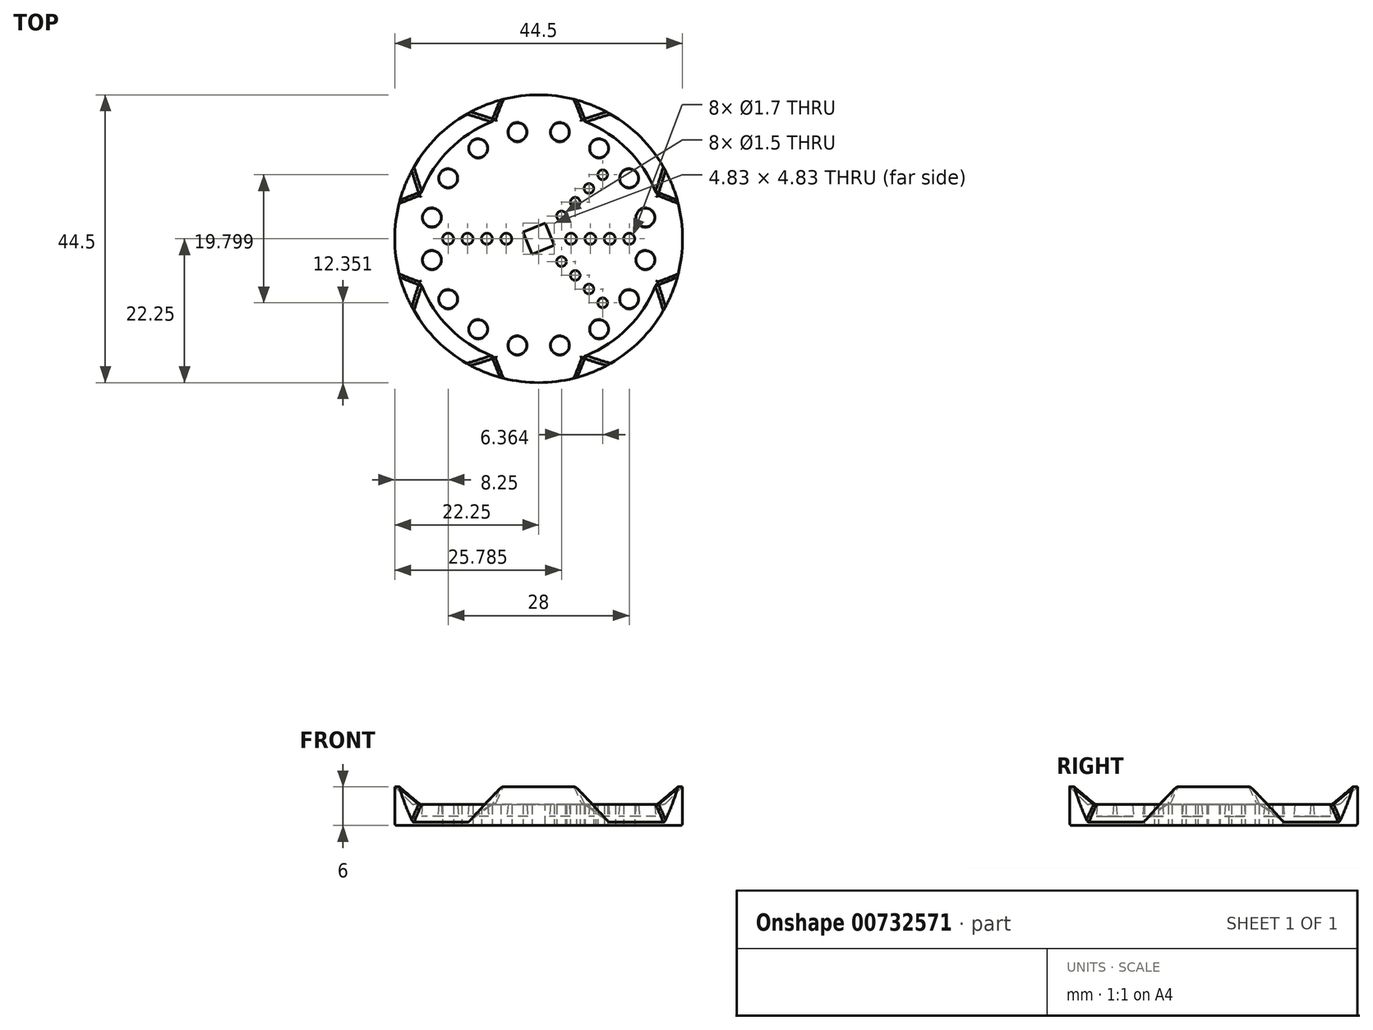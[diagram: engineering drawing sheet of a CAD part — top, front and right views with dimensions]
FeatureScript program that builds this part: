
annotation { "Feature Type Name" : "Feature", "Feature Type Description" : "" }
export const myFeature = defineFeature(function(context is Context, id is Id, definition is map)
    precondition{}
    {
        {
            assignVariable(context, id + "F0", {"name" : "AlignmentGuide", "anyValue" : 2.75});
        }
        {
            assignVariable(context, id + "F1", {"name" : "AlignmentRail", "anyValue" : .5});
        }
        {
            assignVariable(context, id + "F2", {"name" : "AlignmentSpacing", "anyValue" : .25});
        }
        {
            var Q0;
            Q0=qCreatedBy(makeId("Top.planeOp"),FACE);
            var sketch = newSketch(context, id + "F3", { "sketchPlane" : qUnion([Q0])});
            skCircle(sketch, "E0", {"center": v(0, 0) * mm, "radius": 19.5 * mm});
            skCircle(sketch, "E1", {"center": v(5, 0) * mm, "radius": 0.85 * mm});
            skCircle(sketch, "E2", {"center": v(8, 0) * mm, "radius": 0.85 * mm});
            skCircle(sketch, "E3", {"center": v(11, 0) * mm, "radius": 0.85 * mm});
            skCircle(sketch, "E4", {"center": v(14, 0) * mm, "radius": 0.85 * mm});
            skLineSegment(sketch, "E5", {"start": v(2, 0) * mm, "end": v(1.41, 1.41) * mm});
            skLineSegment(sketch, "E6", {"start": v(1.41, -1.41) * mm, "end": v(2, 0) * mm, "construction": true});
            skLineSegment(sketch, "E7", {"start": v(1.7, 0.7) * mm, "end": v(18.02, 7.46) * mm, "construction": true});
            skCircle(sketch, "E8.1.0", {"center": v(-5, 0) * mm, "radius": 0.85 * mm});
            skCircle(sketch, "E8.1.1", {"center": v(-8, 0) * mm, "radius": 0.85 * mm});
            skCircle(sketch, "E8.1.2", {"center": v(-11, 0) * mm, "radius": 0.85 * mm});
            skCircle(sketch, "E8.1.3", {"center": v(-14, 0) * mm, "radius": 0.85 * mm});
            skLineSegment(sketch, "E9", {"start": v(19.5, 0) * mm, "end": v(22.25, 0) * mm, "construction": true});
            skLineSegment(sketch, "E10", {"start": v(18.02, 7.46) * mm, "end": v(17.04, 9.49) * mm, "construction": true});
            skLineSegment(sketch, "E11", {"start": v(18.02, -7.46) * mm, "end": v(17.04, -9.49) * mm, "construction": true});
            skLineSegment(sketch, "E12", {"start": v(17.04, 9.49) * mm, "end": v(19.44, 10.83) * mm});
            skArc(sketch, "E13", {"start": v(19.44, 10.83) * mm, "mid": v(21.54, 5.6) * mm, "end": v(22.25, 0) * mm});
            skLineSegment(sketch, "E14", {"start": v(20.53, 8.86) * mm, "end": v(19.44, 10.83) * mm, "construction": true});
            skArc(sketch, "E15", {"start": v(22.25, 0) * mm, "mid": v(21.54, -5.6) * mm, "end": v(19.44, -10.83) * mm});
            skLineSegment(sketch, "E16", {"start": v(17.04, -9.49) * mm, "end": v(19.44, -10.83) * mm});
            skLineSegment(sketch, "E17", {"start": v(20.53, -8.86) * mm, "end": v(19.44, -10.83) * mm, "construction": true});
            skLineSegment(sketch, "E18", {"start": v(19.44, -10.83) * mm, "end": v(21.84, -12.16) * mm});
            skLineSegment(sketch, "E19", {"start": v(19.44, 10.83) * mm, "end": v(21.84, 12.16) * mm});
            skLineSegment(sketch, "E20", {"start": v(22.25, 0) * mm, "end": v(25, 0) * mm, "construction": true});
            skArc(sketch, "E21", {"start": v(21.84, -12.16) * mm, "mid": v(25, 0) * mm, "end": v(21.84, 12.16) * mm});
            skArc(sketch, "E22", {"start": v(19.44, 10.83) * mm, "mid": v(-22.25, 0) * mm, "end": v(19.44, -10.83) * mm});
            skLineSegment(sketch, "E23", {"start": v(0, 2) * mm, "end": v(0, 19.5) * mm, "construction": true});
            skLineSegment(sketch, "E24", {"start": v(0, 0) * mm, "end": v(0.85, 0) * mm, "construction": true});
            skLineSegment(sketch, "E25", {"start": v(0, 2) * mm, "end": v(1.41, 1.41) * mm, "construction": true});
            skLineSegment(sketch, "E26", {"start": v(0, 0) * mm, "end": v(-0.53, 0.53) * mm, "construction": true});
            skCircle(sketch, "E27", {"center": v(3.54, -3.54) * mm, "radius": 0.75 * mm});
            skLineSegment(sketch, "E28", {"start": v(5, 0) * mm, "end": v(8, 0) * mm, "construction": true});
            skLineSegment(sketch, "E29", {"start": v(8, 0) * mm, "end": v(11, 0) * mm, "construction": true});
            skLineSegment(sketch, "E30", {"start": v(11, 0) * mm, "end": v(14, 0) * mm, "construction": true});
            skLineSegment(sketch, "E31", {"start": v(5, 0) * mm, "end": v(5, 0.85) * mm, "construction": true});
            skLineSegment(sketch, "E32", {"start": v(3.54, -3.54) * mm, "end": v(3, -4.07) * mm, "construction": true});
            skLineSegment(sketch, "E33", {"start": v(3.54, -3.54) * mm, "end": v(5.66, -5.66) * mm, "construction": true});
            skLineSegment(sketch, "E34", {"start": v(5.66, -5.66) * mm, "end": v(7.78, -7.78) * mm, "construction": true});
            skLineSegment(sketch, "E35", {"start": v(7.78, -7.78) * mm, "end": v(9.9, -9.9) * mm, "construction": true});
            skCircle(sketch, "E36", {"center": v(5.66, -5.66) * mm, "radius": 0.75 * mm});
            skCircle(sketch, "E37", {"center": v(7.78, -7.78) * mm, "radius": 0.75 * mm});
            skCircle(sketch, "E38", {"center": v(9.9, -9.9) * mm, "radius": 0.75 * mm});
            skCircle(sketch, "E39.1.0", {"center": v(3.54, 3.54) * mm, "radius": 0.75 * mm});
            skCircle(sketch, "E39.1.1", {"center": v(5.66, 5.66) * mm, "radius": 0.75 * mm});
            skCircle(sketch, "E39.1.2", {"center": v(7.78, 7.78) * mm, "radius": 0.75 * mm});
            skCircle(sketch, "E39.1.3", {"center": v(9.9, 9.9) * mm, "radius": 0.75 * mm});
            skLineSegment(sketch, "E40", {"start": v(2, 0) * mm, "end": v(5, 0) * mm, "construction": true});
            skLineSegment(sketch, "E41", {"start": v(1.41, -1.41) * mm, "end": v(3.54, -3.54) * mm, "construction": true});
            skLineSegment(sketch, "E42", {"start": v(0, 0) * mm, "end": v(0, 2) * mm});
            skLineSegment(sketch, "E43", {"start": v(0, 0) * mm, "end": v(1.41, 1.41) * mm});
            skCircle(sketch, "E44.1.2.0", {"center": v(-3.54, 3.54) * mm, "radius": 0.75 * mm});
            skCircle(sketch, "E44.2.2.0", {"center": v(-5.66, 5.66) * mm, "radius": 0.75 * mm});
            skCircle(sketch, "E44.4.2.0", {"center": v(-7.78, 7.78) * mm, "radius": 0.75 * mm});
            skCircle(sketch, "E44.6.2.0", {"center": v(-9.9, 9.9) * mm, "radius": 0.75 * mm});
            skCircle(sketch, "E44.1.3.0", {"center": v(-3.54, -3.54) * mm, "radius": 0.75 * mm});
            skCircle(sketch, "E44.2.3.0", {"center": v(-5.66, -5.66) * mm, "radius": 0.75 * mm});
            skCircle(sketch, "E44.4.3.0", {"center": v(-7.78, -7.78) * mm, "radius": 0.75 * mm});
            skCircle(sketch, "E44.6.3.0", {"center": v(-9.9, -9.9) * mm, "radius": 0.75 * mm});
            skLineSegment(sketch, "E45", {"start": v(0, 0) * mm, "end": v(0, -2) * mm, "construction": true});
            skLineSegment(sketch, "E46", {"start": v(0, -2) * mm, "end": v(1.41, -1.41) * mm});
            skLineSegment(sketch, "E47", {"start": v(0, 0) * mm, "end": v(1.41, -1.41) * mm, "construction": true});
            skLineSegment(sketch, "E48", {"start": v(1.7, -0.7) * mm, "end": v(18.02, -7.46) * mm, "construction": true});
            skLineSegment(sketch, "E49", {"start": v(0, -2) * mm, "end": v(-1.41, -1.41) * mm, "construction": true});
            skLineSegment(sketch, "E50", {"start": v(-1.41, -1.41) * mm, "end": v(-2, 0) * mm});
            skLineSegment(sketch, "E51", {"start": v(-2, 0) * mm, "end": v(-1.41, 1.41) * mm, "construction": true});
            skLineSegment(sketch, "E52", {"start": v(-1.41, 1.41) * mm, "end": v(0, 2) * mm});
            skLineSegment(sketch, "E53", {"start": v(2, 0) * mm, "end": v(2.41, -1) * mm});
            skLineSegment(sketch, "E54", {"start": v(2.41, -1) * mm, "end": v(1.41, -1.41) * mm});
            skLineSegment(sketch, "E55", {"start": v(0, -2) * mm, "end": v(-1, -2.41) * mm});
            skLineSegment(sketch, "E56", {"start": v(-1, -2.41) * mm, "end": v(-1.41, -1.41) * mm});
            skLineSegment(sketch, "E57", {"start": v(-2, 0) * mm, "end": v(-2.41, 1) * mm});
            skLineSegment(sketch, "E58", {"start": v(-2.41, 1) * mm, "end": v(-1.41, 1.41) * mm});
            skLineSegment(sketch, "E59", {"start": v(0, 2) * mm, "end": v(1, 2.41) * mm});
            skLineSegment(sketch, "E60", {"start": v(1, 2.41) * mm, "end": v(1.41, 1.41) * mm});
            skSolve(sketch);
        }
        {
            var Q0;
            Q0=makeQuery(id+"F3.imprint","IMPRINT",FACE,{"disambiguationData":[TD([[makeQuery(id+"F3.imprint","IMPRINT",EDGE,{"derivedFrom":sQuery(id+"F3.wireOp",EDGE,"E0")}),1.0]])]});
            var Q1;
            Q1=makeQuery(id+"F3.imprint","IMPRINT",FACE,{"disambiguationData":[TD([[makeQuery(id+"F3.imprint","IMPRINT",EDGE,{"derivedFrom":sQuery(id+"F3.wireOp",EDGE,"E1")}),-1.0]])]});
            var Q2;
            {var subQ0=sQuery(id+"F3.wireOp",EDGE,"lLyj6t6n-eD48-rOr1-jQWX-CAubWbmxff8s");Q2=makeQuery(id+"F3.imprint","IMPRINT",FACE,{"disambiguationData":[TD([[makeQuery(id+"F3.imprint","IMPRINT",EDGE,{"derivedFrom":subQ0}),-1.0]])]});}
            var Q3;
            {var subQ0=sQuery(id+"F3.wireOp",EDGE,"lLyj6t6n-eD48-rOr1-jQWX-CAubWbmxff8s");Q3=makeQuery(id+"F3.imprint","IMPRINT",FACE,{"disambiguationData":[TD([[makeQuery(id+"F3.imprint","IMPRINT",EDGE,{"derivedFrom":subQ0}),1.0]])]});}
            var Q4;
            {var subQ0=sQuery(id+"F3.wireOp",EDGE,"E12");Q4=makeQuery(id+"F3.imprint","IMPRINT",FACE,{"disambiguationData":[TD([[makeQuery(id+"F3.imprint","IMPRINT",EDGE,{"derivedFrom":subQ0}),-1.0]])]});}
            var Q5;
            {var subQ0=sQuery(id+"F3.wireOp",EDGE,"E12");Q5=makeQuery(id+"F3.imprint","IMPRINT",FACE,{"disambiguationData":[TD([[makeQuery(id+"F3.imprint","IMPRINT",EDGE,{"derivedFrom":subQ0}),1.0]])]});}
            var Q6;
            {var subQ0=sQuery(id+"F3.wireOp",EDGE,"X5LFDRDO-lWhr-AfW1-3y8W-V0I3BShnL0UQ");Q6=makeQuery(id+"F3.imprint","IMPRINT",FACE,{"disambiguationData":[TD([[makeQuery(id+"F3.imprint","IMPRINT",EDGE,{"derivedFrom":subQ0}),1.0]])]});}
            var Q7;
            {var subQ0=sQuery(id+"F3.wireOp",EDGE,"E42");Q7=makeQuery(id+"F3.imprint","IMPRINT",FACE,{"disambiguationData":[TD([[makeQuery(id+"F3.imprint","IMPRINT",EDGE,{"derivedFrom":subQ0}),-1.0]])]});}
            var Q8;
            Q8=makeQuery(id+"F3.imprint","IMPRINT",FACE,{"disambiguationData":[TD([[makeQuery(id+"F3.imprint","IMPRINT",EDGE,{"derivedFrom":sQuery(id+"F3.wireOp",EDGE,"E44.1.3.0")}),1.0]])]});
            var Q9;
            Q9=makeQuery(id+"F3.imprint","IMPRINT",FACE,{"disambiguationData":[TD([[makeQuery(id+"F3.imprint","IMPRINT",EDGE,{"derivedFrom":sQuery(id+"F3.wireOp",EDGE,"E44.2.3.0")}),1.0]])]});
            var Q10;
            Q10=makeQuery(id+"F3.imprint","IMPRINT",FACE,{"disambiguationData":[TD([[makeQuery(id+"F3.imprint","IMPRINT",EDGE,{"derivedFrom":sQuery(id+"F3.wireOp",EDGE,"E44.4.3.0")}),1.0]])]});
            var Q11;
            Q11=makeQuery(id+"F3.imprint","IMPRINT",FACE,{"disambiguationData":[TD([[makeQuery(id+"F3.imprint","IMPRINT",EDGE,{"derivedFrom":sQuery(id+"F3.wireOp",EDGE,"E44.6.3.0")}),1.0]])]});
            var Q12;
            Q12=makeQuery(id+"F3.imprint","IMPRINT",FACE,{"disambiguationData":[TD([[makeQuery(id+"F3.imprint","IMPRINT",EDGE,{"derivedFrom":sQuery(id+"F3.wireOp",EDGE,"E44.1.2.0")}),1.0]])]});
            var Q13;
            Q13=makeQuery(id+"F3.imprint","IMPRINT",FACE,{"disambiguationData":[TD([[makeQuery(id+"F3.imprint","IMPRINT",EDGE,{"derivedFrom":sQuery(id+"F3.wireOp",EDGE,"E44.6.2.0")}),1.0]])]});
            var Q14;
            Q14=makeQuery(id+"F3.imprint","IMPRINT",FACE,{"disambiguationData":[TD([[makeQuery(id+"F3.imprint","IMPRINT",EDGE,{"derivedFrom":sQuery(id+"F3.wireOp",EDGE,"E44.2.2.0")}),1.0]])]});
            var Q15;
            Q15=makeQuery(id+"F3.imprint","IMPRINT",FACE,{"disambiguationData":[TD([[makeQuery(id+"F3.imprint","IMPRINT",EDGE,{"derivedFrom":sQuery(id+"F3.wireOp",EDGE,"E44.4.2.0")}),1.0]])]});
            extrude(context, id + "F4", {"entities" : qUnion([Q0, Q1, Q2, Q3, Q4, Q5, Q6, Q7, Q8, Q9, Q10, Q11, Q12, Q13, Q14, Q15]), "depth" : (getVariable(context, 'AlignmentGuide') + getVariable(context, 'AlignmentRail')) * mm, "offsetDistance" : 25 * mm});
        }
        {
            var Q0;
            Q0=makeQuery(id+"F4.opExtrude","CAP_EDGE",EDGE,{"disambiguationData":[OSD([sQuery(id+"F3.wireOp",EDGE,"E13"),sQuery(id+"F3.wireOp",EDGE,"E15"),sQuery(id+"F3.wireOp",EDGE,"E22")])],"isStart":false});
            chamfer(context, id + "F5", {"entities" : qUnion([Q0]), "width" : (getVariable(context, 'AlignmentGuide')) * mm, "tangentPropagation" : true});
        }
        {
            var Q0;
            {var subQ0=sQuery(id+"F3.wireOp",EDGE,"E12");Q0=makeQuery(id+"F3.imprint","IMPRINT",FACE,{"disambiguationData":[TD([[makeQuery(id+"F3.imprint","IMPRINT",EDGE,{"derivedFrom":subQ0}),-1.0]])]});}
            var Q1;
            Q1=makeQuery(id+"F3.imprint","IMPRINT",FACE,{"disambiguationData":[TD([[makeQuery(id+"F3.imprint","IMPRINT",EDGE,{"derivedFrom":sQuery(id+"F3.wireOp",EDGE,"E13")}),1.0]])]});
            extrude(context, id + "F6", {"entities" : qUnion([Q0, Q1]), "depth" : (getVariable(context, 'AlignmentSpacing') + getVariable(context, 'AlignmentGuide') * 2 + getVariable(context, 'AlignmentRail') * 2) * mm, "offsetDistance" : 25 * mm});
        }
        {
            var Q0;
            Q0=makeQuery(id+"F6.opExtrude","CAP_EDGE",EDGE,{"disambiguationData":[OSD([sQuery(id+"F3.wireOp",EDGE,"E16"),sQuery(id+"F3.wireOp",EDGE,"E18")])],"isStart":false});
            var Q1;
            Q1=makeQuery(id+"F6.opExtrude","CAP_EDGE",EDGE,{"disambiguationData":[OSD([sQuery(id+"F3.wireOp",EDGE,"E12"),sQuery(id+"F3.wireOp",EDGE,"E19")])],"isStart":false});
            chamfer(context, id + "F7", {"entities" : qUnion([Q0, Q1]), "width" : (getVariable(context, 'AlignmentGuide') * 2 + getVariable(context, 'AlignmentSpacing') + getVariable(context, 'AlignmentRail')) * mm, "tangentPropagation" : true});
        }
        {
            var Q0;
            Q0=makeQuery(id+"F6.opExtrude","CAP_EDGE",EDGE,{"disambiguationData":[OSD([sQuery(id+"F3.wireOp",EDGE,"ykJoU9iX-xNW1-ZPCr-MGLN-cVTnYyaPD16A")])],"isStart":false});
            var Q1;
            Q1=makeQuery(id+"F6.opExtrude","CAP_EDGE",EDGE,{"disambiguationData":[OSD([sQuery(id+"F3.wireOp",EDGE,"lLyj6t6n-eD48-rOr1-jQWX-CAubWbmxff8s")])],"isStart":false});
            var Q2;
            Q2=makeQuery(id+"F6.opExtrude","CAP_EDGE",EDGE,{"disambiguationData":[OSD([sQuery(id+"F3.wireOp",EDGE,"E0")])],"isStart":false});
            chamfer(context, id + "F8", {"entities" : qUnion([Q0, Q1, Q2]), "width" : (getVariable(context, 'AlignmentGuide') + getVariable(context, 'AlignmentSpacing') + getVariable(context, 'AlignmentRail')) * mm, "tangentPropagation" : true});
        }
        {
            var Q0;
            Q0=makeQuery(id+"F8.opChamfer","BLEND_EDGE",EDGE,{"blendedFrom":[makeQuery(id+"F6.opExtrude","CAP_EDGE",EDGE,{"disambiguationData":[OSD([sQuery(id+"F3.wireOp",EDGE,"E0")])],"isStart":false}),makeQuery(id+"F7.opChamfer","BLEND_FACE",FACE,{"disambiguationData":[OSD([sQuery(id+"F3.wireOp",EDGE,"E16"),sQuery(id+"F3.wireOp",EDGE,"E18")])]})],"blendedInto":[makeQuery(id+"F7.opChamfer","BLEND_FACE",FACE,{"disambiguationData":[OSD([sQuery(id+"F3.wireOp",EDGE,"E16"),sQuery(id+"F3.wireOp",EDGE,"E18")])]})]});
            var Q1;
            {var subQ0=sQuery(id+"F3.wireOp",EDGE,"E18");var subQ1=sQuery(id+"F3.wireOp",EDGE,"E16");Q1=makeQuery(id+"F7.opChamfer","BLEND_EDGE",EDGE,{"blendedFrom":[makeQuery(id+"F6.opExtrude","CAP_EDGE",EDGE,{"disambiguationData":[OSD([subQ1,subQ0])],"isStart":false}),makeQuery(id+"F6.opExtrude","CAP_FACE",FACE,{"disambiguationData":[OSD([sQuery(id+"F3.wireOp",EDGE,"E0"),sQuery(id+"F3.wireOp",EDGE,"E12"),subQ1,subQ0,sQuery(id+"F3.wireOp",EDGE,"E19"),sQuery(id+"F3.wireOp",EDGE,"E21")])],"isStart":false})],"blendedInto":[makeQuery(id+"F6.opExtrude","CAP_FACE",FACE,{"disambiguationData":[OSD([sQuery(id+"F3.wireOp",EDGE,"E0"),sQuery(id+"F3.wireOp",EDGE,"E12"),subQ1,subQ0,sQuery(id+"F3.wireOp",EDGE,"E19"),sQuery(id+"F3.wireOp",EDGE,"E21")])],"isStart":false})]});}
            var Q2;
            {var subQ0=sQuery(id+"F3.wireOp",EDGE,"E0");Q2=makeQuery(id+"F8.opChamfer","BLEND_EDGE",EDGE,{"blendedFrom":[makeQuery(id+"F6.opExtrude","CAP_EDGE",EDGE,{"disambiguationData":[OSD([subQ0])],"isStart":false}),makeQuery(id+"F6.opExtrude","CAP_FACE",FACE,{"disambiguationData":[OSD([subQ0,sQuery(id+"F3.wireOp",EDGE,"E12"),sQuery(id+"F3.wireOp",EDGE,"E16"),sQuery(id+"F3.wireOp",EDGE,"E18"),sQuery(id+"F3.wireOp",EDGE,"E19"),sQuery(id+"F3.wireOp",EDGE,"E21")])],"isStart":false})],"blendedInto":[makeQuery(id+"F6.opExtrude","CAP_FACE",FACE,{"disambiguationData":[OSD([subQ0,sQuery(id+"F3.wireOp",EDGE,"E12"),sQuery(id+"F3.wireOp",EDGE,"E16"),sQuery(id+"F3.wireOp",EDGE,"E18"),sQuery(id+"F3.wireOp",EDGE,"E19"),sQuery(id+"F3.wireOp",EDGE,"E21")])],"isStart":false})]});}
            var Q3;
            Q3=makeQuery(id+"F8.opChamfer","BLEND_EDGE",EDGE,{"blendedFrom":[makeQuery(id+"F6.opExtrude","CAP_EDGE",EDGE,{"disambiguationData":[OSD([sQuery(id+"F3.wireOp",EDGE,"E0")])],"isStart":false}),makeQuery(id+"F7.opChamfer","BLEND_FACE",FACE,{"disambiguationData":[OSD([sQuery(id+"F3.wireOp",EDGE,"E12"),sQuery(id+"F3.wireOp",EDGE,"E19")])]})],"blendedInto":[makeQuery(id+"F7.opChamfer","BLEND_FACE",FACE,{"disambiguationData":[OSD([sQuery(id+"F3.wireOp",EDGE,"E12"),sQuery(id+"F3.wireOp",EDGE,"E19")])]})]});
            var Q4;
            {var subQ0=sQuery(id+"F3.wireOp",EDGE,"E19");var subQ1=sQuery(id+"F3.wireOp",EDGE,"E12");Q4=makeQuery(id+"F7.opChamfer","BLEND_EDGE",EDGE,{"blendedFrom":[makeQuery(id+"F6.opExtrude","CAP_EDGE",EDGE,{"disambiguationData":[OSD([subQ1,subQ0])],"isStart":false}),makeQuery(id+"F6.opExtrude","CAP_FACE",FACE,{"disambiguationData":[OSD([sQuery(id+"F3.wireOp",EDGE,"E0"),subQ1,sQuery(id+"F3.wireOp",EDGE,"E16"),sQuery(id+"F3.wireOp",EDGE,"E18"),subQ0,sQuery(id+"F3.wireOp",EDGE,"E21")])],"isStart":false})],"blendedInto":[makeQuery(id+"F6.opExtrude","CAP_FACE",FACE,{"disambiguationData":[OSD([sQuery(id+"F3.wireOp",EDGE,"E0"),subQ1,sQuery(id+"F3.wireOp",EDGE,"E16"),sQuery(id+"F3.wireOp",EDGE,"E18"),subQ0,sQuery(id+"F3.wireOp",EDGE,"E21")])],"isStart":false})]});}
            var Q5;
            Q5=makeQuery(id+"F6.opExtrude","CAP_EDGE",EDGE,{"disambiguationData":[OSD([sQuery(id+"F3.wireOp",EDGE,"E21")])],"isStart":false});
            var Q6;
            Q6=makeQuery(id+"F7.opChamfer","BLEND_EDGE",EDGE,{"blendedFrom":[makeQuery(id+"F6.opExtrude","CAP_EDGE",EDGE,{"disambiguationData":[OSD([sQuery(id+"F3.wireOp",EDGE,"E16"),sQuery(id+"F3.wireOp",EDGE,"E18")])],"isStart":false}),makeQuery(id+"F6.opExtrude","SWEPT_FACE",FACE,{"disambiguationData":[OSD([sQuery(id+"F3.wireOp",EDGE,"E21")])]})],"blendedInto":[makeQuery(id+"F6.opExtrude","SWEPT_FACE",FACE,{"disambiguationData":[OSD([sQuery(id+"F3.wireOp",EDGE,"E21")])]})]});
            var Q7;
            Q7=makeQuery(id+"F7.opChamfer","BLEND_EDGE",EDGE,{"blendedFrom":[makeQuery(id+"F6.opExtrude","CAP_EDGE",EDGE,{"disambiguationData":[OSD([sQuery(id+"F3.wireOp",EDGE,"E12"),sQuery(id+"F3.wireOp",EDGE,"E19")])],"isStart":false}),makeQuery(id+"F6.opExtrude","SWEPT_FACE",FACE,{"disambiguationData":[OSD([sQuery(id+"F3.wireOp",EDGE,"E21")])]})],"blendedInto":[makeQuery(id+"F6.opExtrude","SWEPT_FACE",FACE,{"disambiguationData":[OSD([sQuery(id+"F3.wireOp",EDGE,"E21")])]})]});
            fillet(context, id + "F9", {"entities" : qUnion([Q0, Q1, Q2, Q3, Q4, Q5, Q6, Q7]), "radius" : .5 * mm, "tangentPropagation" : true, "allowEdgeOverflow" : false});
        }
        {
            var Q0;
            Q0=makeQuery(id+"F6.opExtrude","SWEPT_BODY",BODY,{"disambiguationData":[OSD([sQuery(id+"F3.wireOp",EDGE,"E0"),sQuery(id+"F3.wireOp",EDGE,"E12"),sQuery(id+"F3.wireOp",EDGE,"E16"),sQuery(id+"F3.wireOp",EDGE,"E18"),sQuery(id+"F3.wireOp",EDGE,"E19"),sQuery(id+"F3.wireOp",EDGE,"E21")])]});
            var Q1;
            Q1=makeQuery(id+"F4.opExtrude","SWEPT_EDGE",EDGE,{"disambiguationData":[OSD([sQuery(id+"F3.wireOp",EDGE,"E42"),sQuery(id+"F3.wireOp",EDGE,"E43")])]});
            circularPattern(context, id + "F10", {"operationType" : NewBodyOperationType.ADD, "entities" : qUnion([Q0]), "axis" : qUnion([Q1]), "angle" : 360 * degree, "instanceCount" : 4, "equalSpace" : true});
        }
        {
            var Q0;
            {var subQ0=sQuery(id+"F3.wireOp",EDGE,"E42");Q0=makeQuery(id+"F3.imprint","IMPRINT",FACE,{"disambiguationData":[TD([[makeQuery(id+"F3.imprint","IMPRINT",EDGE,{"derivedFrom":subQ0}),-1.0]])]});}
            extrude(context, id + "F11", {"entities" : qUnion([Q0]), "operationType" : NewBodyOperationType.REMOVE, "oppositeDirection" : true, "depth" : 25 * mm, "offsetDistance" : 25 * mm, "hasSecondDirection" : true, "secondDirectionOppositeDirection" : false, "secondDirectionDepth" : 25 * mm});
        }
        {
            var Q0;
            Q0=makeQuery(id+"F10.boolean.opBoolean","INTERSECT",EDGE,{"derivedFrom":[makeQuery(id+"F5.opChamfer","BLEND_FACE",FACE,{"disambiguationData":[OSD([sQuery(id+"F3.wireOp",EDGE,"E13"),sQuery(id+"F3.wireOp",EDGE,"E15"),sQuery(id+"F3.wireOp",EDGE,"E22")])]}),makeQuery(id+"F10.opPattern","COPY",FACE,{"derivedFrom":makeQuery(id+"F7.opChamfer","BLEND_FACE",FACE,{"disambiguationData":[OSD([sQuery(id+"F3.wireOp",EDGE,"E16"),sQuery(id+"F3.wireOp",EDGE,"E18")])]}),"instanceName":"3"})]});
            var Q1;
            Q1=makeQuery(id+"F10.boolean.opBoolean","INTERSECT",EDGE,{"derivedFrom":[makeQuery(id+"F5.opChamfer","BLEND_FACE",FACE,{"disambiguationData":[OSD([sQuery(id+"F3.wireOp",EDGE,"E13"),sQuery(id+"F3.wireOp",EDGE,"E15"),sQuery(id+"F3.wireOp",EDGE,"E22")])]}),makeQuery(id+"F7.opChamfer","BLEND_FACE",FACE,{"disambiguationData":[OSD([sQuery(id+"F3.wireOp",EDGE,"E12"),sQuery(id+"F3.wireOp",EDGE,"E19")])]})]});
            var Q2;
            Q2=makeQuery(id+"F10.boolean.opBoolean","INTERSECT",EDGE,{"derivedFrom":[makeQuery(id+"F5.opChamfer","BLEND_FACE",FACE,{"disambiguationData":[OSD([sQuery(id+"F3.wireOp",EDGE,"E13"),sQuery(id+"F3.wireOp",EDGE,"E15"),sQuery(id+"F3.wireOp",EDGE,"E22")])]}),makeQuery(id+"F7.opChamfer","BLEND_FACE",FACE,{"disambiguationData":[OSD([sQuery(id+"F3.wireOp",EDGE,"E16"),sQuery(id+"F3.wireOp",EDGE,"E18")])]})]});
            var Q3;
            Q3=makeQuery(id+"F10.boolean.opBoolean","INTERSECT",EDGE,{"derivedFrom":[makeQuery(id+"F5.opChamfer","BLEND_FACE",FACE,{"disambiguationData":[OSD([sQuery(id+"F3.wireOp",EDGE,"E13"),sQuery(id+"F3.wireOp",EDGE,"E15"),sQuery(id+"F3.wireOp",EDGE,"E22")])]}),makeQuery(id+"F10.opPattern","COPY",FACE,{"derivedFrom":makeQuery(id+"F7.opChamfer","BLEND_FACE",FACE,{"disambiguationData":[OSD([sQuery(id+"F3.wireOp",EDGE,"E12"),sQuery(id+"F3.wireOp",EDGE,"E19")])]}),"instanceName":"1"})]});
            var Q4;
            Q4=makeQuery(id+"F10.boolean.opBoolean","INTERSECT",EDGE,{"derivedFrom":[makeQuery(id+"F5.opChamfer","BLEND_FACE",FACE,{"disambiguationData":[OSD([sQuery(id+"F3.wireOp",EDGE,"E13"),sQuery(id+"F3.wireOp",EDGE,"E15"),sQuery(id+"F3.wireOp",EDGE,"E22")])]}),makeQuery(id+"F10.opPattern","COPY",FACE,{"derivedFrom":makeQuery(id+"F7.opChamfer","BLEND_FACE",FACE,{"disambiguationData":[OSD([sQuery(id+"F3.wireOp",EDGE,"E16"),sQuery(id+"F3.wireOp",EDGE,"E18")])]}),"instanceName":"1"})]});
            var Q5;
            Q5=makeQuery(id+"F10.boolean.opBoolean","INTERSECT",EDGE,{"derivedFrom":[makeQuery(id+"F5.opChamfer","BLEND_FACE",FACE,{"disambiguationData":[OSD([sQuery(id+"F3.wireOp",EDGE,"E13"),sQuery(id+"F3.wireOp",EDGE,"E15"),sQuery(id+"F3.wireOp",EDGE,"E22")])]}),makeQuery(id+"F10.opPattern","COPY",FACE,{"derivedFrom":makeQuery(id+"F7.opChamfer","BLEND_FACE",FACE,{"disambiguationData":[OSD([sQuery(id+"F3.wireOp",EDGE,"E12"),sQuery(id+"F3.wireOp",EDGE,"E19")])]}),"instanceName":"2"})]});
            var Q6;
            Q6=makeQuery(id+"F10.boolean.opBoolean","INTERSECT",EDGE,{"derivedFrom":[makeQuery(id+"F5.opChamfer","BLEND_FACE",FACE,{"disambiguationData":[OSD([sQuery(id+"F3.wireOp",EDGE,"E13"),sQuery(id+"F3.wireOp",EDGE,"E15"),sQuery(id+"F3.wireOp",EDGE,"E22")])]}),makeQuery(id+"F10.opPattern","COPY",FACE,{"derivedFrom":makeQuery(id+"F7.opChamfer","BLEND_FACE",FACE,{"disambiguationData":[OSD([sQuery(id+"F3.wireOp",EDGE,"E12"),sQuery(id+"F3.wireOp",EDGE,"E19")])]}),"instanceName":"3"})]});
            var Q7;
            Q7=makeQuery(id+"F10.boolean.opBoolean","INTERSECT",EDGE,{"derivedFrom":[makeQuery(id+"F5.opChamfer","BLEND_FACE",FACE,{"disambiguationData":[OSD([sQuery(id+"F3.wireOp",EDGE,"E13"),sQuery(id+"F3.wireOp",EDGE,"E15"),sQuery(id+"F3.wireOp",EDGE,"E22")])]}),makeQuery(id+"F10.opPattern","COPY",FACE,{"derivedFrom":makeQuery(id+"F7.opChamfer","BLEND_FACE",FACE,{"disambiguationData":[OSD([sQuery(id+"F3.wireOp",EDGE,"E16"),sQuery(id+"F3.wireOp",EDGE,"E18")])]}),"instanceName":"2"})]});
            var Q8;
            Q8=makeQuery(id+"F10.boolean.opBoolean","INTERSECT",EDGE,{"derivedFrom":[makeQuery(id+"F4.opExtrude","SWEPT_FACE",FACE,{"disambiguationData":[OSD([sQuery(id+"F3.wireOp",EDGE,"E13"),sQuery(id+"F3.wireOp",EDGE,"E15"),sQuery(id+"F3.wireOp",EDGE,"E22")])]}),makeQuery(id+"F10.opPattern","COPY",FACE,{"derivedFrom":makeQuery(id+"F6.opExtrude","SWEPT_FACE",FACE,{"disambiguationData":[OSD([sQuery(id+"F3.wireOp",EDGE,"E16"),sQuery(id+"F3.wireOp",EDGE,"E18")])]}),"instanceName":"2"})]});
            var Q9;
            Q9=makeQuery(id+"F10.boolean.opBoolean","INTERSECT",EDGE,{"derivedFrom":[makeQuery(id+"F4.opExtrude","SWEPT_FACE",FACE,{"disambiguationData":[OSD([sQuery(id+"F3.wireOp",EDGE,"E13"),sQuery(id+"F3.wireOp",EDGE,"E15"),sQuery(id+"F3.wireOp",EDGE,"E22")])]}),makeQuery(id+"F10.opPattern","COPY",FACE,{"derivedFrom":makeQuery(id+"F6.opExtrude","SWEPT_FACE",FACE,{"disambiguationData":[OSD([sQuery(id+"F3.wireOp",EDGE,"E12"),sQuery(id+"F3.wireOp",EDGE,"E19")])]}),"instanceName":"3"})]});
            var Q10;
            Q10=makeQuery(id+"F10.boolean.opBoolean","INTERSECT",EDGE,{"derivedFrom":[makeQuery(id+"F4.opExtrude","SWEPT_FACE",FACE,{"disambiguationData":[OSD([sQuery(id+"F3.wireOp",EDGE,"E13"),sQuery(id+"F3.wireOp",EDGE,"E15"),sQuery(id+"F3.wireOp",EDGE,"E22")])]}),makeQuery(id+"F10.opPattern","COPY",FACE,{"derivedFrom":makeQuery(id+"F6.opExtrude","SWEPT_FACE",FACE,{"disambiguationData":[OSD([sQuery(id+"F3.wireOp",EDGE,"E12"),sQuery(id+"F3.wireOp",EDGE,"E19")])]}),"instanceName":"2"})]});
            var Q11;
            Q11=makeQuery(id+"F10.boolean.opBoolean","INTERSECT",EDGE,{"derivedFrom":[makeQuery(id+"F4.opExtrude","SWEPT_FACE",FACE,{"disambiguationData":[OSD([sQuery(id+"F3.wireOp",EDGE,"E13"),sQuery(id+"F3.wireOp",EDGE,"E15"),sQuery(id+"F3.wireOp",EDGE,"E22")])]}),makeQuery(id+"F10.opPattern","COPY",FACE,{"derivedFrom":makeQuery(id+"F6.opExtrude","SWEPT_FACE",FACE,{"disambiguationData":[OSD([sQuery(id+"F3.wireOp",EDGE,"E16"),sQuery(id+"F3.wireOp",EDGE,"E18")])]}),"instanceName":"1"})]});
            var Q12;
            Q12=makeQuery(id+"F10.boolean.opBoolean","INTERSECT",EDGE,{"derivedFrom":[makeQuery(id+"F4.opExtrude","SWEPT_FACE",FACE,{"disambiguationData":[OSD([sQuery(id+"F3.wireOp",EDGE,"E13"),sQuery(id+"F3.wireOp",EDGE,"E15"),sQuery(id+"F3.wireOp",EDGE,"E22")])]}),makeQuery(id+"F6.opExtrude","SWEPT_FACE",FACE,{"disambiguationData":[OSD([sQuery(id+"F3.wireOp",EDGE,"E16"),sQuery(id+"F3.wireOp",EDGE,"E18")])]})]});
            var Q13;
            Q13=makeQuery(id+"F10.boolean.opBoolean","INTERSECT",EDGE,{"derivedFrom":[makeQuery(id+"F4.opExtrude","SWEPT_FACE",FACE,{"disambiguationData":[OSD([sQuery(id+"F3.wireOp",EDGE,"E13"),sQuery(id+"F3.wireOp",EDGE,"E15"),sQuery(id+"F3.wireOp",EDGE,"E22")])]}),makeQuery(id+"F10.opPattern","COPY",FACE,{"derivedFrom":makeQuery(id+"F6.opExtrude","SWEPT_FACE",FACE,{"disambiguationData":[OSD([sQuery(id+"F3.wireOp",EDGE,"E12"),sQuery(id+"F3.wireOp",EDGE,"E19")])]}),"instanceName":"1"})]});
            var Q14;
            Q14=makeQuery(id+"F10.boolean.opBoolean","INTERSECT",EDGE,{"derivedFrom":[makeQuery(id+"F4.opExtrude","SWEPT_FACE",FACE,{"disambiguationData":[OSD([sQuery(id+"F3.wireOp",EDGE,"E13"),sQuery(id+"F3.wireOp",EDGE,"E15"),sQuery(id+"F3.wireOp",EDGE,"E22")])]}),makeQuery(id+"F10.opPattern","COPY",FACE,{"derivedFrom":makeQuery(id+"F6.opExtrude","SWEPT_FACE",FACE,{"disambiguationData":[OSD([sQuery(id+"F3.wireOp",EDGE,"E16"),sQuery(id+"F3.wireOp",EDGE,"E18")])]}),"instanceName":"3"})]});
            var Q15;
            Q15=makeQuery(id+"F10.boolean.opBoolean","INTERSECT",EDGE,{"derivedFrom":[makeQuery(id+"F4.opExtrude","SWEPT_FACE",FACE,{"disambiguationData":[OSD([sQuery(id+"F3.wireOp",EDGE,"E13"),sQuery(id+"F3.wireOp",EDGE,"E15"),sQuery(id+"F3.wireOp",EDGE,"E22")])]}),makeQuery(id+"F6.opExtrude","SWEPT_FACE",FACE,{"disambiguationData":[OSD([sQuery(id+"F3.wireOp",EDGE,"E12"),sQuery(id+"F3.wireOp",EDGE,"E19")])]})]});
            fillet(context, id + "F12", {"entities" : qUnion([Q0, Q1, Q2, Q3, Q4, Q5, Q6, Q7, Q8, Q9, Q10, Q11, Q12, Q13, Q14, Q15]), "radius" : .5 * mm, "tangentPropagation" : true, "allowEdgeOverflow" : false});
        }
        {
            var Q0;
            {var subQ0=sQuery(id+"F3.wireOp",EDGE,"E18");var subQ1=sQuery(id+"F3.wireOp",EDGE,"E16");var subQ2=sQuery(id+"F3.wireOp",EDGE,"E22");var subQ3=sQuery(id+"F3.wireOp",EDGE,"E15");var subQ4=sQuery(id+"F3.wireOp",EDGE,"E13");var subQ5=makeQuery(id+"F4.opExtrude","SWEPT_FACE",FACE,{"disambiguationData":[OSD([subQ4,subQ3,subQ2])]});Q0=makeQuery(id+"F10.boolean.opBoolean","SPLIT",EDGE,{"disambiguationData":[TD([makeQuery(id+"F10.opPattern","COPY",FACE,{"derivedFrom":makeQuery(id+"F6.opExtrude","SWEPT_FACE",FACE,{"disambiguationData":[OSD([subQ1,subQ0])]}),"instanceName":"2"})])],"derivedFrom":makeQuery(id+"F5.opChamfer","BLEND_EDGE",EDGE,{"blendedFrom":[makeQuery(id+"F4.opExtrude","CAP_EDGE",EDGE,{"disambiguationData":[OSD([subQ4,subQ3,subQ2])],"isStart":false}),subQ5],"blendedInto":[subQ5]})});}
            var Q1;
            Q1=makeQuery(id+"F10.opPattern","COPY",EDGE,{"derivedFrom":makeQuery(id+"F6.opExtrude","SWEPT_EDGE",EDGE,{"disambiguationData":[OSD([sQuery(id+"F3.wireOp",EDGE,"E18"),sQuery(id+"F3.wireOp",EDGE,"E21")])]}),"instanceName":"2"});
            var Q2;
            {var subQ1=sQuery(id+"F3.wireOp",EDGE,"E18");var subQ2=sQuery(id+"F3.wireOp",EDGE,"E16");var subQ5=sQuery(id+"F3.wireOp",EDGE,"E22");var subQ6=sQuery(id+"F3.wireOp",EDGE,"E15");var subQ7=sQuery(id+"F3.wireOp",EDGE,"E13");Q2=makeQuery(id+"F10.boolean.opBoolean","SPLIT",EDGE,{"disambiguationData":[TD([makeQuery(id+"F10.opPattern","COPY",FACE,{"derivedFrom":makeQuery(id+"F6.opExtrude","SWEPT_FACE",FACE,{"disambiguationData":[OSD([subQ2,subQ1])]}),"instanceName":"2"})])],"derivedFrom":makeQuery(id+"F4.opExtrude","CAP_EDGE",EDGE,{"disambiguationData":[OSD([subQ7,subQ6,subQ5])],"isStart":true})});}
            var Q3;
            Q3=makeQuery(id+"F10.opPattern","COPY",EDGE,{"derivedFrom":makeQuery(id+"F6.opExtrude","CAP_EDGE",EDGE,{"disambiguationData":[OSD([sQuery(id+"F3.wireOp",EDGE,"E21")])],"isStart":true}),"instanceName":"2"});
            var Q4;
            Q4=makeQuery(id+"F10.opPattern","COPY",EDGE,{"derivedFrom":makeQuery(id+"F6.opExtrude","CAP_EDGE",EDGE,{"disambiguationData":[OSD([sQuery(id+"F3.wireOp",EDGE,"E21")])],"isStart":true}),"instanceName":"3"});
            var Q5;
            Q5=makeQuery(id+"F10.opPattern","COPY",EDGE,{"derivedFrom":makeQuery(id+"F6.opExtrude","SWEPT_EDGE",EDGE,{"disambiguationData":[OSD([sQuery(id+"F3.wireOp",EDGE,"E19"),sQuery(id+"F3.wireOp",EDGE,"E21")])]}),"instanceName":"3"});
            var Q6;
            {var subQ0=sQuery(id+"F3.wireOp",EDGE,"E19");var subQ1=sQuery(id+"F3.wireOp",EDGE,"E12");var subQ5=sQuery(id+"F3.wireOp",EDGE,"E22");var subQ6=sQuery(id+"F3.wireOp",EDGE,"E15");var subQ7=sQuery(id+"F3.wireOp",EDGE,"E13");Q6=makeQuery(id+"F10.boolean.opBoolean","SPLIT",EDGE,{"disambiguationData":[TD([makeQuery(id+"F6.opExtrude","SWEPT_FACE",FACE,{"disambiguationData":[OSD([subQ1,subQ0])]})])],"derivedFrom":makeQuery(id+"F4.opExtrude","CAP_EDGE",EDGE,{"disambiguationData":[OSD([subQ7,subQ6,subQ5])],"isStart":true})});}
            var Q7;
            Q7=makeQuery(id+"F10.opPattern","COPY",EDGE,{"derivedFrom":makeQuery(id+"F6.opExtrude","SWEPT_EDGE",EDGE,{"disambiguationData":[OSD([sQuery(id+"F3.wireOp",EDGE,"E18"),sQuery(id+"F3.wireOp",EDGE,"E21")])]}),"instanceName":"3"});
            var Q8;
            Q8=makeQuery(id+"F6.opExtrude","SWEPT_EDGE",EDGE,{"disambiguationData":[OSD([sQuery(id+"F3.wireOp",EDGE,"E19"),sQuery(id+"F3.wireOp",EDGE,"E21")])]});
            var Q9;
            Q9=makeQuery(id+"F6.opExtrude","SWEPT_EDGE",EDGE,{"disambiguationData":[OSD([sQuery(id+"F3.wireOp",EDGE,"E18"),sQuery(id+"F3.wireOp",EDGE,"E21")])]});
            var Q10;
            Q10=makeQuery(id+"F10.opPattern","COPY",EDGE,{"derivedFrom":makeQuery(id+"F6.opExtrude","SWEPT_EDGE",EDGE,{"disambiguationData":[OSD([sQuery(id+"F3.wireOp",EDGE,"E19"),sQuery(id+"F3.wireOp",EDGE,"E21")])]}),"instanceName":"1"});
            var Q11;
            {var subQ1=sQuery(id+"F3.wireOp",EDGE,"E18");var subQ2=sQuery(id+"F3.wireOp",EDGE,"E16");var subQ5=sQuery(id+"F3.wireOp",EDGE,"E22");var subQ6=sQuery(id+"F3.wireOp",EDGE,"E15");var subQ7=sQuery(id+"F3.wireOp",EDGE,"E13");Q11=makeQuery(id+"F10.boolean.opBoolean","SPLIT",EDGE,{"disambiguationData":[TD([makeQuery(id+"F6.opExtrude","SWEPT_FACE",FACE,{"disambiguationData":[OSD([subQ2,subQ1])]})])],"derivedFrom":makeQuery(id+"F4.opExtrude","CAP_EDGE",EDGE,{"disambiguationData":[OSD([subQ7,subQ6,subQ5])],"isStart":true})});}
            var Q12;
            Q12=makeQuery(id+"F6.opExtrude","CAP_EDGE",EDGE,{"disambiguationData":[OSD([sQuery(id+"F3.wireOp",EDGE,"E21")])],"isStart":true});
            var Q13;
            Q13=makeQuery(id+"F10.opPattern","COPY",EDGE,{"derivedFrom":makeQuery(id+"F6.opExtrude","CAP_EDGE",EDGE,{"disambiguationData":[OSD([sQuery(id+"F3.wireOp",EDGE,"E21")])],"isStart":true}),"instanceName":"1"});
            var Q14;
            {var subQ1=sQuery(id+"F3.wireOp",EDGE,"E18");var subQ2=sQuery(id+"F3.wireOp",EDGE,"E16");var subQ5=sQuery(id+"F3.wireOp",EDGE,"E22");var subQ6=sQuery(id+"F3.wireOp",EDGE,"E15");var subQ7=sQuery(id+"F3.wireOp",EDGE,"E13");Q14=makeQuery(id+"F10.boolean.opBoolean","SPLIT",EDGE,{"disambiguationData":[TD([makeQuery(id+"F10.opPattern","COPY",FACE,{"derivedFrom":makeQuery(id+"F6.opExtrude","SWEPT_FACE",FACE,{"disambiguationData":[OSD([subQ2,subQ1])]}),"instanceName":"1"})])],"derivedFrom":makeQuery(id+"F4.opExtrude","CAP_EDGE",EDGE,{"disambiguationData":[OSD([subQ7,subQ6,subQ5])],"isStart":true})});}
            var Q15;
            Q15=makeQuery(id+"F10.opPattern","COPY",EDGE,{"derivedFrom":makeQuery(id+"F6.opExtrude","SWEPT_EDGE",EDGE,{"disambiguationData":[OSD([sQuery(id+"F3.wireOp",EDGE,"E18"),sQuery(id+"F3.wireOp",EDGE,"E21")])]}),"instanceName":"1"});
            var Q16;
            Q16=makeQuery(id+"F10.opPattern","COPY",EDGE,{"derivedFrom":makeQuery(id+"F6.opExtrude","SWEPT_EDGE",EDGE,{"disambiguationData":[OSD([sQuery(id+"F3.wireOp",EDGE,"E19"),sQuery(id+"F3.wireOp",EDGE,"E21")])]}),"instanceName":"2"});
            var Q17;
            {var subQ0=sQuery(id+"F3.wireOp",EDGE,"E19");var subQ1=sQuery(id+"F3.wireOp",EDGE,"E12");var subQ2=sQuery(id+"F3.wireOp",EDGE,"E22");var subQ3=sQuery(id+"F3.wireOp",EDGE,"E15");var subQ4=sQuery(id+"F3.wireOp",EDGE,"E13");var subQ5=makeQuery(id+"F4.opExtrude","SWEPT_FACE",FACE,{"disambiguationData":[OSD([subQ4,subQ3,subQ2])]});Q17=makeQuery(id+"F10.boolean.opBoolean","SPLIT",EDGE,{"disambiguationData":[TD([makeQuery(id+"F6.opExtrude","SWEPT_FACE",FACE,{"disambiguationData":[OSD([subQ1,subQ0])]})])],"derivedFrom":makeQuery(id+"F5.opChamfer","BLEND_EDGE",EDGE,{"blendedFrom":[makeQuery(id+"F4.opExtrude","CAP_EDGE",EDGE,{"disambiguationData":[OSD([subQ4,subQ3,subQ2])],"isStart":false}),subQ5],"blendedInto":[subQ5]})});}
            var Q18;
            {var subQ0=sQuery(id+"F3.wireOp",EDGE,"E18");var subQ1=sQuery(id+"F3.wireOp",EDGE,"E16");var subQ2=sQuery(id+"F3.wireOp",EDGE,"E22");var subQ3=sQuery(id+"F3.wireOp",EDGE,"E15");var subQ4=sQuery(id+"F3.wireOp",EDGE,"E13");var subQ5=makeQuery(id+"F4.opExtrude","SWEPT_FACE",FACE,{"disambiguationData":[OSD([subQ4,subQ3,subQ2])]});Q18=makeQuery(id+"F10.boolean.opBoolean","SPLIT",EDGE,{"disambiguationData":[TD([makeQuery(id+"F6.opExtrude","SWEPT_FACE",FACE,{"disambiguationData":[OSD([subQ1,subQ0])]})])],"derivedFrom":makeQuery(id+"F5.opChamfer","BLEND_EDGE",EDGE,{"blendedFrom":[makeQuery(id+"F4.opExtrude","CAP_EDGE",EDGE,{"disambiguationData":[OSD([subQ4,subQ3,subQ2])],"isStart":false}),subQ5],"blendedInto":[subQ5]})});}
            var Q19;
            {var subQ0=sQuery(id+"F3.wireOp",EDGE,"E18");var subQ1=sQuery(id+"F3.wireOp",EDGE,"E16");var subQ2=sQuery(id+"F3.wireOp",EDGE,"E22");var subQ3=sQuery(id+"F3.wireOp",EDGE,"E15");var subQ4=sQuery(id+"F3.wireOp",EDGE,"E13");var subQ5=makeQuery(id+"F4.opExtrude","SWEPT_FACE",FACE,{"disambiguationData":[OSD([subQ4,subQ3,subQ2])]});Q19=makeQuery(id+"F10.boolean.opBoolean","SPLIT",EDGE,{"disambiguationData":[TD([makeQuery(id+"F10.opPattern","COPY",FACE,{"derivedFrom":makeQuery(id+"F6.opExtrude","SWEPT_FACE",FACE,{"disambiguationData":[OSD([subQ1,subQ0])]}),"instanceName":"1"})])],"derivedFrom":makeQuery(id+"F5.opChamfer","BLEND_EDGE",EDGE,{"blendedFrom":[makeQuery(id+"F4.opExtrude","CAP_EDGE",EDGE,{"disambiguationData":[OSD([subQ4,subQ3,subQ2])],"isStart":false}),subQ5],"blendedInto":[subQ5]})});}
            fillet(context, id + "F13", {"entities" : qUnion([Q0, Q1, Q2, Q3, Q4, Q5, Q6, Q7, Q8, Q9, Q10, Q11, Q12, Q13, Q14, Q15, Q16, Q17, Q18, Q19]), "radius" : .35 * mm, "tangentPropagation" : true, "allowEdgeOverflow" : false});
        }
        {
            var Q0;
            Q0=makeQuery(id+"F4.opExtrude","CAP_FACE",FACE,{"disambiguationData":[OSD([sQuery(id+"F3.wireOp",EDGE,"E1"),sQuery(id+"F3.wireOp",EDGE,"E2"),sQuery(id+"F3.wireOp",EDGE,"E3"),sQuery(id+"F3.wireOp",EDGE,"E4"),sQuery(id+"F3.wireOp",EDGE,"nXEHubGE-ARxO-8yHd-py5p-j8Clxyko91KH"),sQuery(id+"F3.wireOp",EDGE,"E8.1.0"),sQuery(id+"F3.wireOp",EDGE,"E8.1.1"),sQuery(id+"F3.wireOp",EDGE,"E8.1.2"),sQuery(id+"F3.wireOp",EDGE,"E8.1.3"),sQuery(id+"F3.wireOp",EDGE,"E13"),sQuery(id+"F3.wireOp",EDGE,"E15"),sQuery(id+"F3.wireOp",EDGE,"E22"),sQuery(id+"F3.wireOp",EDGE,"E27"),sQuery(id+"F3.wireOp",EDGE,"E36"),sQuery(id+"F3.wireOp",EDGE,"E37"),sQuery(id+"F3.wireOp",EDGE,"E38"),sQuery(id+"F3.wireOp",EDGE,"E42"),sQuery(id+"F3.wireOp",EDGE,"E43"),sQuery(id+"F3.wireOp",EDGE,"E44.1.3.0"),sQuery(id+"F3.wireOp",EDGE,"E44.2.3.0"),sQuery(id+"F3.wireOp",EDGE,"E44.4.3.0"),sQuery(id+"F3.wireOp",EDGE,"E44.6.3.0")])],"isStart":false});
            var sketch = newSketch(context, id + "F14", { "sketchPlane" : qUnion([Q0])});
            skCircle(sketch, "E61", {"center": v(16.5, -3.28) * mm, "radius": 1.45 * mm});
            skLineSegment(sketch, "E62", {"start": v(16.5, -3.28) * mm, "end": v(15.05, -3.28) * mm, "construction": true});
            skCircle(sketch, "E63.1.0", {"center": v(16.5, 3.28) * mm, "radius": 1.45 * mm});
            skCircle(sketch, "E63.2.0", {"center": v(13.99, 9.35) * mm, "radius": 1.45 * mm});
            skCircle(sketch, "E63.3.0", {"center": v(9.35, 13.99) * mm, "radius": 1.45 * mm});
            skCircle(sketch, "E63.4.0", {"center": v(3.28, 16.5) * mm, "radius": 1.45 * mm});
            skCircle(sketch, "E63.5.0", {"center": v(-3.28, 16.5) * mm, "radius": 1.45 * mm});
            skCircle(sketch, "E63.6.0", {"center": v(-9.35, 13.99) * mm, "radius": 1.45 * mm});
            skCircle(sketch, "E63.7.0", {"center": v(-13.99, 9.35) * mm, "radius": 1.45 * mm});
            skPoint(sketch, "E63.center", {"position": v(0, 0) * mm});
            skCircle(sketch, "E64.1.8.0", {"center": v(-16.5, 3.28) * mm, "radius": 1.45 * mm});
            skCircle(sketch, "E64.1.9.0", {"center": v(-16.5, -3.28) * mm, "radius": 1.45 * mm});
            skCircle(sketch, "E64.1.10.0", {"center": v(-13.99, -9.35) * mm, "radius": 1.45 * mm});
            skCircle(sketch, "E64.1.11.0", {"center": v(-9.35, -13.99) * mm, "radius": 1.45 * mm});
            skCircle(sketch, "E64.1.12.0", {"center": v(-3.28, -16.5) * mm, "radius": 1.45 * mm});
            skCircle(sketch, "E64.1.13.0", {"center": v(3.28, -16.5) * mm, "radius": 1.45 * mm});
            skCircle(sketch, "E64.1.14.0", {"center": v(9.35, -13.99) * mm, "radius": 1.45 * mm});
            skCircle(sketch, "E64.1.15.0", {"center": v(13.99, -9.35) * mm, "radius": 1.45 * mm});
            skLineSegment(sketch, "E65", {"start": v(16.5, 3.28) * mm, "end": v(16.5, -3.28) * mm, "construction": true});
            skLineSegment(sketch, "E66", {"start": v(16.5, 0) * mm, "end": v(14, 0) * mm, "construction": true});
            skLineSegment(sketch, "E67", {"start": v(14, 0) * mm, "end": v(0, 0) * mm, "construction": true});
            skSolve(sketch);
        }
        {
            var Q0;
            Q0=makeQuery(id+"F14.imprint","IMPRINT",FACE,{"disambiguationData":[TD([[makeQuery(id+"F14.imprint","IMPRINT",EDGE,{"derivedFrom":sQuery(id+"F14.wireOp",EDGE,"E63.3.0")}),1.0]])]});
            var Q1;
            Q1=makeQuery(id+"F14.imprint","IMPRINT",FACE,{"disambiguationData":[TD([[makeQuery(id+"F14.imprint","IMPRINT",EDGE,{"derivedFrom":sQuery(id+"F14.wireOp",EDGE,"E63.2.0")}),1.0]])]});
            var Q2;
            Q2=makeQuery(id+"F14.imprint","IMPRINT",FACE,{"disambiguationData":[TD([[makeQuery(id+"F14.imprint","IMPRINT",EDGE,{"derivedFrom":sQuery(id+"F14.wireOp",EDGE,"E61")}),1.0]])]});
            var Q3;
            Q3=makeQuery(id+"F14.imprint","IMPRINT",FACE,{"disambiguationData":[TD([[makeQuery(id+"F14.imprint","IMPRINT",EDGE,{"derivedFrom":sQuery(id+"F14.wireOp",EDGE,"E63.1.0")}),1.0]])]});
            var Q4;
            Q4=makeQuery(id+"F14.imprint","IMPRINT",FACE,{"disambiguationData":[TD([[makeQuery(id+"F14.imprint","IMPRINT",EDGE,{"derivedFrom":sQuery(id+"F14.wireOp",EDGE,"E63.4.0")}),1.0]])]});
            var Q5;
            Q5=makeQuery(id+"F14.imprint","IMPRINT",FACE,{"disambiguationData":[TD([[makeQuery(id+"F14.imprint","IMPRINT",EDGE,{"derivedFrom":sQuery(id+"F14.wireOp",EDGE,"E63.5.0")}),1.0]])]});
            var Q6;
            Q6=makeQuery(id+"F14.imprint","IMPRINT",FACE,{"disambiguationData":[TD([[makeQuery(id+"F14.imprint","IMPRINT",EDGE,{"derivedFrom":sQuery(id+"F14.wireOp",EDGE,"E63.6.0")}),1.0]])]});
            var Q7;
            Q7=makeQuery(id+"F14.imprint","IMPRINT",FACE,{"disambiguationData":[TD([[makeQuery(id+"F14.imprint","IMPRINT",EDGE,{"derivedFrom":sQuery(id+"F14.wireOp",EDGE,"E63.7.0")}),1.0]])]});
            var Q8;
            Q8=makeQuery(id+"F14.imprint","IMPRINT",FACE,{"disambiguationData":[TD([[makeQuery(id+"F14.imprint","IMPRINT",EDGE,{"derivedFrom":sQuery(id+"F14.wireOp",EDGE,"E64.1.8.0")}),1.0]])]});
            var Q9;
            Q9=makeQuery(id+"F14.imprint","IMPRINT",FACE,{"disambiguationData":[TD([[makeQuery(id+"F14.imprint","IMPRINT",EDGE,{"derivedFrom":sQuery(id+"F14.wireOp",EDGE,"E64.1.9.0")}),1.0]])]});
            var Q10;
            Q10=makeQuery(id+"F14.imprint","IMPRINT",FACE,{"disambiguationData":[TD([[makeQuery(id+"F14.imprint","IMPRINT",EDGE,{"derivedFrom":sQuery(id+"F14.wireOp",EDGE,"E64.1.10.0")}),1.0]])]});
            var Q11;
            Q11=makeQuery(id+"F14.imprint","IMPRINT",FACE,{"disambiguationData":[TD([[makeQuery(id+"F14.imprint","IMPRINT",EDGE,{"derivedFrom":sQuery(id+"F14.wireOp",EDGE,"E64.1.11.0")}),1.0]])]});
            var Q12;
            Q12=makeQuery(id+"F14.imprint","IMPRINT",FACE,{"disambiguationData":[TD([[makeQuery(id+"F14.imprint","IMPRINT",EDGE,{"derivedFrom":sQuery(id+"F14.wireOp",EDGE,"E64.1.12.0")}),1.0]])]});
            var Q13;
            Q13=makeQuery(id+"F14.imprint","IMPRINT",FACE,{"disambiguationData":[TD([[makeQuery(id+"F14.imprint","IMPRINT",EDGE,{"derivedFrom":sQuery(id+"F14.wireOp",EDGE,"E64.1.13.0")}),1.0]])]});
            var Q14;
            Q14=makeQuery(id+"F14.imprint","IMPRINT",FACE,{"disambiguationData":[TD([[makeQuery(id+"F14.imprint","IMPRINT",EDGE,{"derivedFrom":sQuery(id+"F14.wireOp",EDGE,"E64.1.14.0")}),1.0]])]});
            var Q15;
            Q15=makeQuery(id+"F14.imprint","IMPRINT",FACE,{"disambiguationData":[TD([[makeQuery(id+"F14.imprint","IMPRINT",EDGE,{"derivedFrom":sQuery(id+"F14.wireOp",EDGE,"E64.1.15.0")}),1.0]])]});
            extrude(context, id + "F15", {"entities" : qUnion([Q0, Q1, Q2, Q3, Q4, Q5, Q6, Q7, Q8, Q9, Q10, Q11, Q12, Q13, Q14, Q15]), "operationType" : NewBodyOperationType.REMOVE, "oppositeDirection" : true, "depth" : 1.8 * mm, "offsetDistance" : 25 * mm, "hasDraft" : true, "draftAngle" : 5 * degree});
        }
    });
